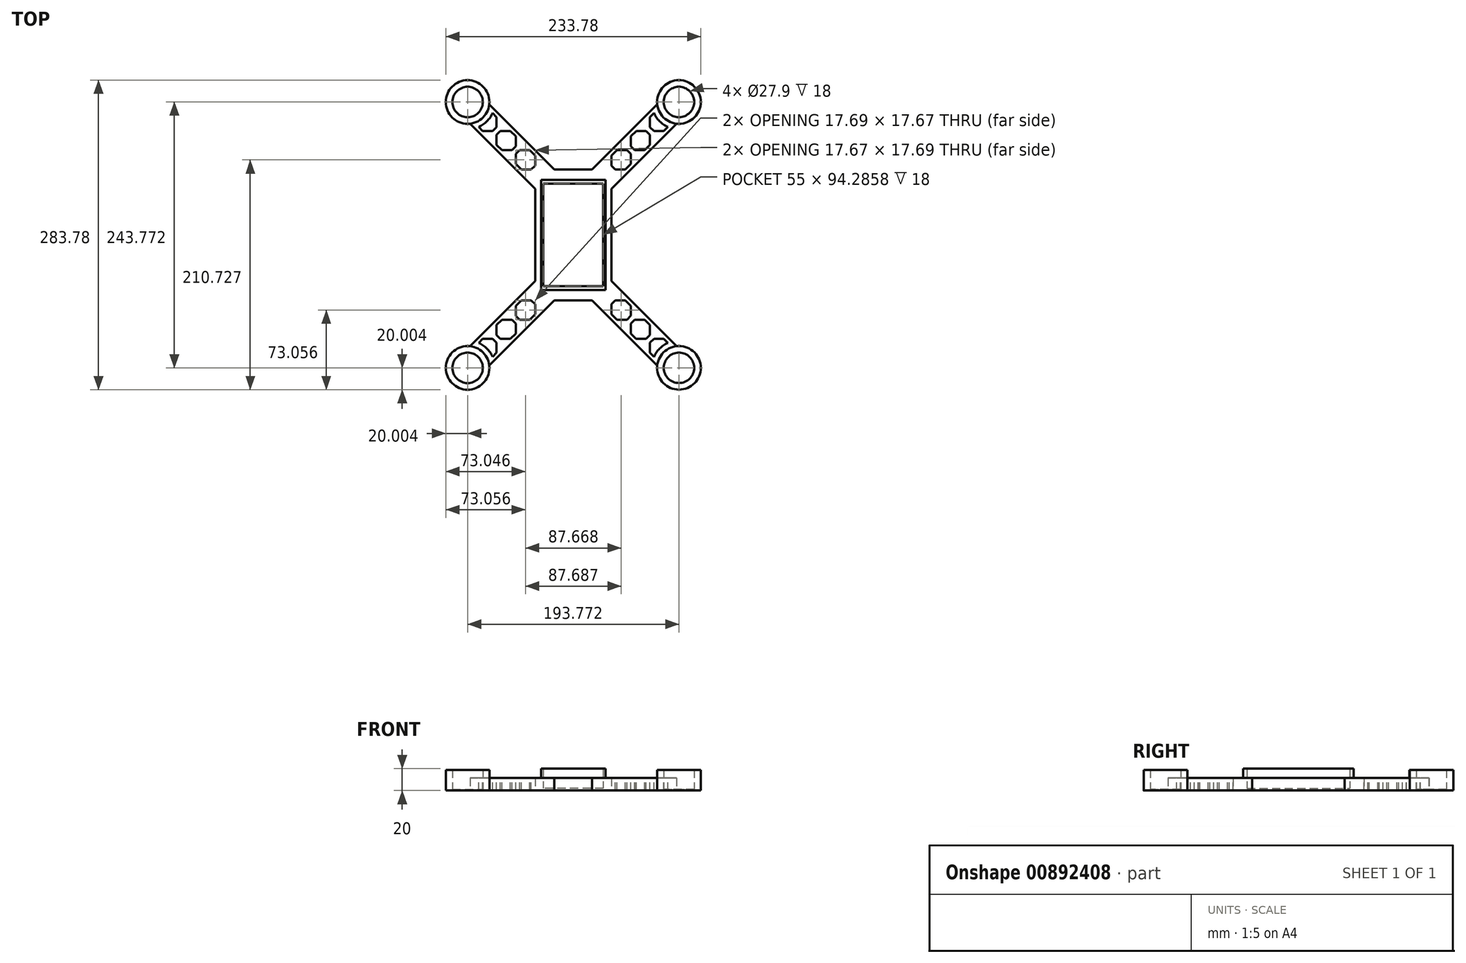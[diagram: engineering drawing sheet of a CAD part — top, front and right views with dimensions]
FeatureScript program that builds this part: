
annotation { "Feature Type Name" : "Feature", "Feature Type Description" : "" }
export const myFeature = defineFeature(function(context is Context, id is Id, definition is map)
    precondition{}
    {
        {
            var Q0;
            Q0=qCreatedBy(makeId("Top.planeOp"),FACE);
            var sketch = newSketch(context, id + "F0", { "sketchPlane" : qUnion([Q0])});
            skLineSegment(sketch, "E0.bottom", {"start": v(-35, 60) * mm, "end": v(35, 60) * mm});
            skLineSegment(sketch, "E0.top", {"start": v(-35, -60) * mm, "end": v(35, -60) * mm});
            skLineSegment(sketch, "E0.left", {"start": v(-35, 60) * mm, "end": v(-35, -60) * mm});
            skLineSegment(sketch, "E0.right", {"start": v(35, 60) * mm, "end": v(35, -60) * mm});
            skPoint(sketch, "E0.middle", {"position": v(0, 0) * mm});
            skPoint(sketch, "E1.middle", {"position": v(-35, 60) * mm});
            skLineSegment(sketch, "E2", {"start": v(-35, 60) * mm, "end": v(35, -60) * mm, "construction": true});
            skLineSegment(sketch, "E3", {"start": v(-35, -60) * mm, "end": v(35, 60) * mm, "construction": true});
            skLineSegment(sketch, "E4", {"start": v(-27.5, 47.14) * mm, "end": v(27.5, 47.14) * mm});
            skLineSegment(sketch, "E5", {"start": v(-27.5, -47.14) * mm, "end": v(27.5, -47.14) * mm});
            skLineSegment(sketch, "E6", {"start": v(27.5, 47.14) * mm, "end": v(27.5, -47.14) * mm});
            skLineSegment(sketch, "E7", {"start": v(-27.5, 47.14) * mm, "end": v(-27.5, -47.14) * mm});
            skPoint(sketch, "E8", {"position": v(-29.52, 50.6) * mm});
            skLineSegment(sketch, "E9", {"start": v(-29.52, 50.6) * mm, "end": v(-29.52, -50.6) * mm});
            skLineSegment(sketch, "E10", {"start": v(-29.52, -50.6) * mm, "end": v(29.52, -50.6) * mm});
            skLineSegment(sketch, "E11", {"start": v(29.52, -50.6) * mm, "end": v(29.52, 50.6) * mm});
            skLineSegment(sketch, "E12", {"start": v(29.52, 50.6) * mm, "end": v(-29.52, 50.6) * mm});
            skLineSegment(sketch, "E13", {"start": v(35, 60) * mm, "end": v(-35, 11.89) * mm, "construction": true});
            skLineSegment(sketch, "E14", {"start": v(35, 11.89) * mm, "end": v(-35, 131.89) * mm, "construction": true});
            skLineSegment(sketch, "E15", {"start": v(-17.33, -60) * mm, "end": v(-35, -42.32) * mm});
            skLineSegment(sketch, "E16", {"start": v(-35, -42.32) * mm, "end": v(-105.72, -113.02) * mm});
            skLineSegment(sketch, "E17", {"start": v(-105.72, -113.02) * mm, "end": v(-88.05, -130.7) * mm});
            skLineSegment(sketch, "E18", {"start": v(-88.05, -130.7) * mm, "end": v(-17.33, -60) * mm});
            skLineSegment(sketch, "E19", {"start": v(105.72, 113.02) * mm, "end": v(88.05, 130.7) * mm});
            skLineSegment(sketch, "E20", {"start": v(88.05, 130.7) * mm, "end": v(17.33, 60) * mm});
            skLineSegment(sketch, "E21", {"start": v(17.33, 60) * mm, "end": v(35, 42.32) * mm});
            skLineSegment(sketch, "E22", {"start": v(35, 42.32) * mm, "end": v(105.72, 113.02) * mm});
            skLineSegment(sketch, "E23", {"start": v(88.05, -130.7) * mm, "end": v(105.72, -113.02) * mm});
            skLineSegment(sketch, "E24", {"start": v(105.72, -113.02) * mm, "end": v(35, -42.32) * mm});
            skLineSegment(sketch, "E25", {"start": v(35, -42.32) * mm, "end": v(17.33, -60) * mm});
            skLineSegment(sketch, "E26", {"start": v(17.33, -60) * mm, "end": v(88.05, -130.7) * mm});
            skLineSegment(sketch, "E27", {"start": v(-35, 42.32) * mm, "end": v(-17.33, 60) * mm});
            skLineSegment(sketch, "E28", {"start": v(-17.33, 60) * mm, "end": v(-88.05, 130.7) * mm});
            skLineSegment(sketch, "E29", {"start": v(-88.05, 130.7) * mm, "end": v(-105.72, 113.02) * mm});
            skLineSegment(sketch, "E30", {"start": v(-105.72, 113.02) * mm, "end": v(-35, 42.32) * mm});
            skLineSegment(sketch, "E31", {"start": v(-35, 42.32) * mm, "end": v(-35, -42.32) * mm});
            skLineSegment(sketch, "E32", {"start": v(-17.33, 60) * mm, "end": v(17.33, 60) * mm});
            skLineSegment(sketch, "E33", {"start": v(35, 42.32) * mm, "end": v(35, -42.32) * mm});
            skSolve(sketch);
        }
        {
            var Q0;
            Q0 = qSketchRegion(id + "F0", true);
            extrude(context, id + "F1", {"entities" : qUnion([Q0]), "depth" : 10 * mm, "offsetDistance" : 25 * mm});
        }
        {
            var Q0;
            Q0=makeQuery(id+"F0.imprint","IMPRINT",FACE,{"disambiguationData":[TD([[makeQuery(id+"F0.imprint","IMPRINT",EDGE,{"derivedFrom":sQuery(id+"F0.wireOp",EDGE,"E4")}),1.0]])]});
            var Q1;
            {var subQ0=sQuery(id+"F0.wireOp",EDGE,"E12");var subQ1=sQuery(id+"F0.wireOp",EDGE,"E9");var subQ2=makeQuery(id+"F0.imprint","INTERSECT",VERTEX,{"derivedFrom":[subQ1,subQ0]});Q1=makeQuery(id+"F0.imprint","IMPRINT",FACE,{"disambiguationData":[TD([[makeQuery(id+"F0.imprint","IMPRINT",EDGE,{"disambiguationData":[TD([[subQ2,-1.0]])],"derivedFrom":subQ1}),1.0]])]});}
            var Q2;
            {var subQ0=sQuery(id+"F0.wireOp",EDGE,"E12");var subQ1=sQuery(id+"F0.wireOp",EDGE,"E11");var subQ2=makeQuery(id+"F0.imprint","INTERSECT",VERTEX,{"derivedFrom":[subQ1,subQ0]});Q2=makeQuery(id+"F0.imprint","IMPRINT",FACE,{"disambiguationData":[TD([[makeQuery(id+"F0.imprint","IMPRINT",EDGE,{"disambiguationData":[TD([[subQ2,1.0]])],"derivedFrom":subQ1}),1.0]])]});}
            var Q3;
            {var subQ0=sQuery(id+"F0.wireOp",EDGE,"E11");var subQ1=sQuery(id+"F0.wireOp",EDGE,"E10");var subQ2=makeQuery(id+"F0.imprint","INTERSECT",VERTEX,{"derivedFrom":[subQ1,subQ0]});Q3=makeQuery(id+"F0.imprint","IMPRINT",FACE,{"disambiguationData":[TD([[makeQuery(id+"F0.imprint","IMPRINT",EDGE,{"disambiguationData":[TD([[subQ2,1.0]])],"derivedFrom":subQ1}),1.0]])]});}
            var Q4;
            {var subQ0=sQuery(id+"F0.wireOp",EDGE,"E10");var subQ1=sQuery(id+"F0.wireOp",EDGE,"E9");var subQ2=makeQuery(id+"F0.imprint","INTERSECT",VERTEX,{"derivedFrom":[subQ1,subQ0]});Q4=makeQuery(id+"F0.imprint","IMPRINT",FACE,{"disambiguationData":[TD([[makeQuery(id+"F0.imprint","IMPRINT",EDGE,{"disambiguationData":[TD([[subQ2,1.0]])],"derivedFrom":subQ1}),1.0]])]});}
            extrude(context, id + "F2", {"entities" : qUnion([Q0, Q1, Q2, Q3, Q4]), "operationType" : NewBodyOperationType.ADD, "depth" : 20 * mm, "offsetDistance" : 25 * mm});
        }
        {
            var Q0;
            Q0=makeQuery(id+"F0.imprint","IMPRINT",FACE,{"disambiguationData":[TD([[makeQuery(id+"F0.imprint","IMPRINT",EDGE,{"derivedFrom":sQuery(id+"F0.wireOp",EDGE,"E4")}),-1.0]])]});
            extrude(context, id + "F3", {"entities" : qUnion([Q0]), "operationType" : NewBodyOperationType.ADD, "depth" : 3 * mm, "offsetDistance" : 25 * mm});
        }
        {
            var Q0;
            {var subQ0=sQuery(id+"F0.wireOp",EDGE,"E7");var subQ1=sQuery(id+"F0.wireOp",EDGE,"E6");var subQ2=sQuery(id+"F0.wireOp",EDGE,"E5");var subQ3=sQuery(id+"F0.wireOp",EDGE,"E4");var subQ4=sQuery(id+"F0.wireOp",EDGE,"E12");var subQ5=sQuery(id+"F0.wireOp",EDGE,"E11");var subQ6=sQuery(id+"F0.wireOp",EDGE,"E10");var subQ7=sQuery(id+"F0.wireOp",EDGE,"E9");Q0=makeQuery(id+"F3.boolean.opBoolean","MERGE",FACE,{"derivedFrom":[makeQuery(id+"F2.boolean.opBoolean","MERGE",FACE,{"derivedFrom":[makeQuery(id+"F1.opExtrude","CAP_FACE",FACE,{"disambiguationData":[OSD([sQuery(id+"F0.wireOp",EDGE,"E0.top"),subQ7,subQ6,subQ5,subQ4,sQuery(id+"F0.wireOp",EDGE,"E16"),sQuery(id+"F0.wireOp",EDGE,"E17"),sQuery(id+"F0.wireOp",EDGE,"E18"),sQuery(id+"F0.wireOp",EDGE,"E19"),sQuery(id+"F0.wireOp",EDGE,"E20"),sQuery(id+"F0.wireOp",EDGE,"E22"),sQuery(id+"F0.wireOp",EDGE,"E23"),sQuery(id+"F0.wireOp",EDGE,"E24"),sQuery(id+"F0.wireOp",EDGE,"E26"),sQuery(id+"F0.wireOp",EDGE,"E28"),sQuery(id+"F0.wireOp",EDGE,"E29"),sQuery(id+"F0.wireOp",EDGE,"E30"),sQuery(id+"F0.wireOp",EDGE,"E31"),sQuery(id+"F0.wireOp",EDGE,"E32"),sQuery(id+"F0.wireOp",EDGE,"E33")])],"isStart":true}),makeQuery(id+"F2.opExtrude","CAP_FACE",FACE,{"disambiguationData":[OSD([subQ3,subQ2,subQ1,subQ0,subQ7,subQ6,subQ5,subQ4])],"isStart":true})]}),makeQuery(id+"F3.opExtrude","CAP_FACE",FACE,{"disambiguationData":[OSD([subQ3,subQ2,subQ1,subQ0])],"isStart":true})]});}
            var sketch = newSketch(context, id + "F4", { "sketchPlane" : qUnion([Q0])});
            skLineSegment(sketch, "E34", {"start": v(-35, 42.32) * mm, "end": v(35, 42.32) * mm, "construction": true});
            skLineSegment(sketch, "E35", {"start": v(35, -42.32) * mm, "end": v(-35, -42.32) * mm, "construction": true});
            skLineSegment(sketch, "E36", {"start": v(0, 42.32) * mm, "end": v(0, -42.32) * mm, "construction": true});
            skLineSegment(sketch, "E37", {"start": v(-30, 42.32) * mm, "end": v(-30, -42.32) * mm});
            skLineSegment(sketch, "E38", {"start": v(-30, -42.32) * mm, "end": v(-27, -42.32) * mm, "construction": true});
            skLineSegment(sketch, "E39", {"start": v(-27, -42.32) * mm, "end": v(-27, 42.32) * mm});
            skLineSegment(sketch, "E40", {"start": v(-27, 42.32) * mm, "end": v(-30, 42.32) * mm});
            skLineSegment(sketch, "E41", {"start": v(-30, -42.32) * mm, "end": v(-27, -42.32) * mm});
            skLineSegment(sketch, "E42.MirrorCS", {"start": v(30, 42.32) * mm, "end": v(30, -42.32) * mm});
            skLineSegment(sketch, "E43.MirrorCS", {"start": v(27, -42.32) * mm, "end": v(27, 42.32) * mm});
            skLineSegment(sketch, "E44", {"start": v(30, 42.32) * mm, "end": v(27, 42.32) * mm});
            skLineSegment(sketch, "E45", {"start": v(27, -42.32) * mm, "end": v(30, -42.32) * mm});
            skSolve(sketch);
        }
        {
            var Q0;
            {var subQ0=sQuery(id+"F0.wireOp",EDGE,"E7");var subQ1=sQuery(id+"F0.wireOp",EDGE,"E6");var subQ2=sQuery(id+"F0.wireOp",EDGE,"E5");var subQ3=sQuery(id+"F0.wireOp",EDGE,"E4");var subQ4=sQuery(id+"F0.wireOp",EDGE,"E12");var subQ5=sQuery(id+"F0.wireOp",EDGE,"E11");var subQ6=sQuery(id+"F0.wireOp",EDGE,"E10");var subQ7=sQuery(id+"F0.wireOp",EDGE,"E9");Q0=makeQuery(id+"F3.boolean.opBoolean","MERGE",FACE,{"derivedFrom":[makeQuery(id+"F2.boolean.opBoolean","MERGE",FACE,{"derivedFrom":[makeQuery(id+"F1.opExtrude","CAP_FACE",FACE,{"disambiguationData":[OSD([sQuery(id+"F0.wireOp",EDGE,"E0.top"),subQ7,subQ6,subQ5,subQ4,sQuery(id+"F0.wireOp",EDGE,"E16"),sQuery(id+"F0.wireOp",EDGE,"E17"),sQuery(id+"F0.wireOp",EDGE,"E18"),sQuery(id+"F0.wireOp",EDGE,"E19"),sQuery(id+"F0.wireOp",EDGE,"E20"),sQuery(id+"F0.wireOp",EDGE,"E22"),sQuery(id+"F0.wireOp",EDGE,"E23"),sQuery(id+"F0.wireOp",EDGE,"E24"),sQuery(id+"F0.wireOp",EDGE,"E26"),sQuery(id+"F0.wireOp",EDGE,"E28"),sQuery(id+"F0.wireOp",EDGE,"E29"),sQuery(id+"F0.wireOp",EDGE,"E30"),sQuery(id+"F0.wireOp",EDGE,"E31"),sQuery(id+"F0.wireOp",EDGE,"E32"),sQuery(id+"F0.wireOp",EDGE,"E33")])],"isStart":true}),makeQuery(id+"F2.opExtrude","CAP_FACE",FACE,{"disambiguationData":[OSD([subQ3,subQ2,subQ1,subQ0,subQ7,subQ6,subQ5,subQ4])],"isStart":true})]}),makeQuery(id+"F3.opExtrude","CAP_FACE",FACE,{"disambiguationData":[OSD([subQ3,subQ2,subQ1,subQ0])],"isStart":true})]});}
            var sketch = newSketch(context, id + "F5", { "sketchPlane" : qUnion([Q0])});
            skCircle(sketch, "E46", {"center": v(96.89, 121.86) * mm, "radius": 13.95 * mm});
            skCircle(sketch, "E47", {"center": v(96.89, 121.86) * mm, "radius": 20 * mm});
            skLineSegment(sketch, "E48", {"start": v(88.05, 130.7) * mm, "end": v(111.03, 107.71) * mm, "construction": true});
            skCircle(sketch, "E49", {"center": v(-96.86, 121.89) * mm, "radius": 13.95 * mm});
            skCircle(sketch, "E50", {"center": v(-96.86, 121.89) * mm, "radius": 20 * mm});
            skCircle(sketch, "E51", {"center": v(96.86, -121.89) * mm, "radius": 13.95 * mm});
            skCircle(sketch, "E52", {"center": v(96.86, -121.89) * mm, "radius": 20 * mm});
            skCircle(sketch, "E53", {"center": v(-96.89, -121.86) * mm, "radius": 13.95 * mm});
            skCircle(sketch, "E54", {"center": v(-96.89, -121.86) * mm, "radius": 20 * mm});
            skSolve(sketch);
        }
        {
            var Q0;
            {var subQ0=sQuery(id+"F5.wireOp",EDGE,"47fc8cb0-7b7c-463f-8738-2b292fe60b7a0.MirrorCS");var subQ1=sQuery(id+"F5.wireOp",EDGE,"E47");var subQ2=makeQuery(id+"F5.imprint","INTERSECT",VERTEX,{"disambiguationData":[OD(1.0)],"derivedFrom":[subQ1,subQ0]});Q0=makeQuery(id+"F5.imprint","IMPRINT",FACE,{"disambiguationData":[TD([[makeQuery(id+"F5.imprint","IMPRINT",EDGE,{"disambiguationData":[TD([[subQ2,-1.0]])],"derivedFrom":subQ1}),-1.0]])]});}
            var Q1;
            {var subQ0=sQuery(id+"F5.wireOp",EDGE,"VyiwcckC-eZpB-Ns7w-MLVF-TjthNmdLp171");var subQ1=sQuery(id+"F5.wireOp",EDGE,"E47");var subQ2=makeQuery(id+"F5.imprint","INTERSECT",VERTEX,{"disambiguationData":[OD(1.0)],"derivedFrom":[subQ1,subQ0]});Q1=makeQuery(id+"F5.imprint","IMPRINT",FACE,{"disambiguationData":[TD([[makeQuery(id+"F5.imprint","IMPRINT",EDGE,{"disambiguationData":[TD([[subQ2,1.0]])],"derivedFrom":subQ1}),-1.0]])]});}
            var Q2;
            {var subQ6=makeQuery(id+"F1.opExtrude","CAP_EDGE",EDGE,{"disambiguationData":[OSD([sQuery(id+"F0.wireOp",EDGE,"E24")])],"isStart":true});var subQ11=sQuery(id+"F5.wireOp",EDGE,"E46");var subQ12=makeQuery(id+"F5.imprint","INTERSECT",VERTEX,{"derivedFrom":[subQ6,subQ11]});Q2=makeQuery(id+"F5.imprint","IMPRINT",FACE,{"disambiguationData":[TD([[makeQuery(id+"F5.imprint","IMPRINT",EDGE,{"disambiguationData":[TD([[subQ12,-1.0]])],"derivedFrom":subQ11}),-1.0]])]});}
            var Q3;
            {var subQ0=sQuery(id+"F5.wireOp",EDGE,"E46");var subQ1=makeQuery(id+"F1.opExtrude","CAP_EDGE",EDGE,{"disambiguationData":[OSD([sQuery(id+"F0.wireOp",EDGE,"E24")])],"isStart":true});var subQ2=makeQuery(id+"F5.imprint","INTERSECT",VERTEX,{"derivedFrom":[subQ1,subQ0]});Q3=makeQuery(id+"F5.imprint","IMPRINT",FACE,{"disambiguationData":[TD([[makeQuery(id+"F5.imprint","IMPRINT",EDGE,{"disambiguationData":[TD([[subQ2,1.0]])],"derivedFrom":subQ0}),-1.0]])]});}
            extrude(context, id + "F6", {"entities" : qUnion([Q0, Q1, Q2, Q3]), "operationType" : NewBodyOperationType.ADD, "depth" : -18 * mm, "offsetDistance" : 25 * mm});
        }
        {
            var Q0;
            {var subQ8=sQuery(id+"F5.wireOp",EDGE,"E49");var subQ11=makeQuery(id+"F1.opExtrude","CAP_EDGE",EDGE,{"disambiguationData":[OSD([sQuery(id+"F0.wireOp",EDGE,"E16")])],"isStart":true});var subQ13=makeQuery(id+"F5.imprint","INTERSECT",VERTEX,{"derivedFrom":[subQ11,subQ8]});Q0=makeQuery(id+"F5.imprint","IMPRINT",FACE,{"disambiguationData":[TD([[makeQuery(id+"F5.imprint","IMPRINT",EDGE,{"disambiguationData":[TD([[subQ13,1.0]])],"derivedFrom":subQ8}),-1.0]])]});}
            var Q1;
            {var subQ0=sQuery(id+"F5.wireOp",EDGE,"3d39e784-e424-4d79-a023-b1c7c5447e9a.MirrorCS");var subQ1=sQuery(id+"F5.wireOp",EDGE,"E50");var subQ2=makeQuery(id+"F5.imprint","INTERSECT",VERTEX,{"disambiguationData":[OD(1.0)],"derivedFrom":[subQ1,subQ0]});Q1=makeQuery(id+"F5.imprint","IMPRINT",FACE,{"disambiguationData":[TD([[makeQuery(id+"F5.imprint","IMPRINT",EDGE,{"disambiguationData":[TD([[subQ2,-1.0]])],"derivedFrom":subQ1}),-1.0]])]});}
            var Q2;
            {var subQ0=sQuery(id+"F5.wireOp",EDGE,"9ff1a962-2a44-446a-a701-eef2fafc3d29");var subQ1=sQuery(id+"F5.wireOp",EDGE,"E50");var subQ2=makeQuery(id+"F5.imprint","INTERSECT",VERTEX,{"disambiguationData":[OD(1.0)],"derivedFrom":[subQ1,subQ0]});Q2=makeQuery(id+"F5.imprint","IMPRINT",FACE,{"disambiguationData":[TD([[makeQuery(id+"F5.imprint","IMPRINT",EDGE,{"disambiguationData":[TD([[subQ2,1.0]])],"derivedFrom":subQ1}),-1.0]])]});}
            var Q3;
            {var subQ0=sQuery(id+"F5.wireOp",EDGE,"E49");var subQ1=makeQuery(id+"F1.opExtrude","CAP_EDGE",EDGE,{"disambiguationData":[OSD([sQuery(id+"F0.wireOp",EDGE,"E16")])],"isStart":true});var subQ2=makeQuery(id+"F5.imprint","INTERSECT",VERTEX,{"derivedFrom":[subQ1,subQ0]});Q3=makeQuery(id+"F5.imprint","IMPRINT",FACE,{"disambiguationData":[TD([[makeQuery(id+"F5.imprint","IMPRINT",EDGE,{"disambiguationData":[TD([[subQ2,-1.0]])],"derivedFrom":subQ0}),-1.0]])]});}
            var Q4;
            {var subQ0=sQuery(id+"F5.wireOp",EDGE,"47fc8cb0-7b7c-463f-8738-2b292fe60b7a0.MirrorCS");var subQ1=sQuery(id+"F5.wireOp",EDGE,"E47");var subQ2=makeQuery(id+"F5.imprint","INTERSECT",VERTEX,{"disambiguationData":[OD(1.0)],"derivedFrom":[subQ1,subQ0]});Q4=makeQuery(id+"F5.imprint","IMPRINT",FACE,{"disambiguationData":[TD([[makeQuery(id+"F5.imprint","IMPRINT",EDGE,{"disambiguationData":[TD([[subQ2,-1.0]])],"derivedFrom":subQ1}),-1.0]])]});}
            var Q5;
            {var subQ0=sQuery(id+"F5.wireOp",EDGE,"E46");var subQ1=makeQuery(id+"F1.opExtrude","CAP_EDGE",EDGE,{"disambiguationData":[OSD([sQuery(id+"F0.wireOp",EDGE,"E24")])],"isStart":true});var subQ2=makeQuery(id+"F5.imprint","INTERSECT",VERTEX,{"derivedFrom":[subQ1,subQ0]});Q5=makeQuery(id+"F5.imprint","IMPRINT",FACE,{"disambiguationData":[TD([[makeQuery(id+"F5.imprint","IMPRINT",EDGE,{"disambiguationData":[TD([[subQ2,1.0]])],"derivedFrom":subQ0}),-1.0]])]});}
            var Q6;
            {var subQ0=sQuery(id+"F5.wireOp",EDGE,"VyiwcckC-eZpB-Ns7w-MLVF-TjthNmdLp171");var subQ1=sQuery(id+"F5.wireOp",EDGE,"E47");var subQ2=makeQuery(id+"F5.imprint","INTERSECT",VERTEX,{"disambiguationData":[OD(1.0)],"derivedFrom":[subQ1,subQ0]});Q6=makeQuery(id+"F5.imprint","IMPRINT",FACE,{"disambiguationData":[TD([[makeQuery(id+"F5.imprint","IMPRINT",EDGE,{"disambiguationData":[TD([[subQ2,1.0]])],"derivedFrom":subQ1}),-1.0]])]});}
            var Q7;
            {var subQ7=sQuery(id+"F5.wireOp",EDGE,"E46");var subQ10=makeQuery(id+"F1.opExtrude","CAP_EDGE",EDGE,{"disambiguationData":[OSD([sQuery(id+"F0.wireOp",EDGE,"E24")])],"isStart":true});var subQ13=makeQuery(id+"F5.imprint","INTERSECT",VERTEX,{"derivedFrom":[subQ10,subQ7]});Q7=makeQuery(id+"F5.imprint","IMPRINT",FACE,{"disambiguationData":[TD([[makeQuery(id+"F5.imprint","IMPRINT",EDGE,{"disambiguationData":[TD([[subQ13,-1.0]])],"derivedFrom":subQ7}),-1.0]])]});}
            var Q8;
            {var subQ6=makeQuery(id+"F1.opExtrude","CAP_EDGE",EDGE,{"disambiguationData":[OSD([sQuery(id+"F0.wireOp",EDGE,"E20")])],"isStart":true});var subQ11=sQuery(id+"F5.wireOp",EDGE,"E51");var subQ12=makeQuery(id+"F5.imprint","INTERSECT",VERTEX,{"derivedFrom":[subQ6,subQ11]});Q8=makeQuery(id+"F5.imprint","IMPRINT",FACE,{"disambiguationData":[TD([[makeQuery(id+"F5.imprint","IMPRINT",EDGE,{"disambiguationData":[TD([[subQ12,-1.0]])],"derivedFrom":subQ11}),-1.0]])]});}
            var Q9;
            {var subQ0=sQuery(id+"F5.wireOp",EDGE,"E51");var subQ1=makeQuery(id+"F1.opExtrude","CAP_EDGE",EDGE,{"disambiguationData":[OSD([sQuery(id+"F0.wireOp",EDGE,"E20")])],"isStart":true});var subQ2=makeQuery(id+"F5.imprint","INTERSECT",VERTEX,{"derivedFrom":[subQ1,subQ0]});Q9=makeQuery(id+"F5.imprint","IMPRINT",FACE,{"disambiguationData":[TD([[makeQuery(id+"F5.imprint","IMPRINT",EDGE,{"disambiguationData":[TD([[subQ2,1.0]])],"derivedFrom":subQ0}),-1.0]])]});}
            var Q10;
            {var subQ0=sQuery(id+"F5.wireOp",EDGE,"61715c0d-76a2-4f19-8c7d-4868fa988be3");var subQ1=sQuery(id+"F5.wireOp",EDGE,"E52");var subQ2=makeQuery(id+"F5.imprint","INTERSECT",VERTEX,{"disambiguationData":[OD(1.0)],"derivedFrom":[subQ1,subQ0]});Q10=makeQuery(id+"F5.imprint","IMPRINT",FACE,{"disambiguationData":[TD([[makeQuery(id+"F5.imprint","IMPRINT",EDGE,{"disambiguationData":[TD([[subQ2,1.0]])],"derivedFrom":subQ1}),-1.0]])]});}
            var Q11;
            {var subQ0=sQuery(id+"F5.wireOp",EDGE,"6347a85b-d320-4235-87b3-466630833275.MirrorCS");var subQ1=sQuery(id+"F5.wireOp",EDGE,"E52");var subQ2=makeQuery(id+"F5.imprint","INTERSECT",VERTEX,{"disambiguationData":[OD(1.0)],"derivedFrom":[subQ1,subQ0]});Q11=makeQuery(id+"F5.imprint","IMPRINT",FACE,{"disambiguationData":[TD([[makeQuery(id+"F5.imprint","IMPRINT",EDGE,{"disambiguationData":[TD([[subQ2,-1.0]])],"derivedFrom":subQ1}),-1.0]])]});}
            var Q12;
            {var subQ0=sQuery(id+"F5.wireOp",EDGE,"E53");var subQ1=makeQuery(id+"F1.opExtrude","CAP_EDGE",EDGE,{"disambiguationData":[OSD([sQuery(id+"F0.wireOp",EDGE,"E28")])],"isStart":true});var subQ2=makeQuery(id+"F5.imprint","INTERSECT",VERTEX,{"derivedFrom":[subQ1,subQ0]});Q12=makeQuery(id+"F5.imprint","IMPRINT",FACE,{"disambiguationData":[TD([[makeQuery(id+"F5.imprint","IMPRINT",EDGE,{"disambiguationData":[TD([[subQ2,-1.0]])],"derivedFrom":subQ0}),-1.0]])]});}
            var Q13;
            {var subQ0=sQuery(id+"F5.wireOp",EDGE,"2b9b2cda-c36c-46c9-b2f3-9b1550c60cb7.MirrorCS");var subQ1=sQuery(id+"F5.wireOp",EDGE,"E54");var subQ2=makeQuery(id+"F5.imprint","INTERSECT",VERTEX,{"disambiguationData":[OD(1.0)],"derivedFrom":[subQ1,subQ0]});Q13=makeQuery(id+"F5.imprint","IMPRINT",FACE,{"disambiguationData":[TD([[makeQuery(id+"F5.imprint","IMPRINT",EDGE,{"disambiguationData":[TD([[subQ2,-1.0]])],"derivedFrom":subQ1}),-1.0]])]});}
            var Q14;
            {var subQ8=makeQuery(id+"F1.opExtrude","CAP_EDGE",EDGE,{"disambiguationData":[OSD([sQuery(id+"F0.wireOp",EDGE,"E28")])],"isStart":true});var subQ10=sQuery(id+"F5.wireOp",EDGE,"E53");var subQ11=makeQuery(id+"F5.imprint","INTERSECT",VERTEX,{"derivedFrom":[subQ8,subQ10]});Q14=makeQuery(id+"F5.imprint","IMPRINT",FACE,{"disambiguationData":[TD([[makeQuery(id+"F5.imprint","IMPRINT",EDGE,{"disambiguationData":[TD([[subQ11,1.0]])],"derivedFrom":subQ10}),-1.0]])]});}
            var Q15;
            {var subQ0=sQuery(id+"F5.wireOp",EDGE,"51958e25-218a-4250-a5e8-a469592214fb");var subQ1=sQuery(id+"F5.wireOp",EDGE,"E54");var subQ2=makeQuery(id+"F5.imprint","INTERSECT",VERTEX,{"disambiguationData":[OD(1.0)],"derivedFrom":[subQ1,subQ0]});Q15=makeQuery(id+"F5.imprint","IMPRINT",FACE,{"disambiguationData":[TD([[makeQuery(id+"F5.imprint","IMPRINT",EDGE,{"disambiguationData":[TD([[subQ2,1.0]])],"derivedFrom":subQ1}),-1.0]])]});}
            extrude(context, id + "F7", {"entities" : qUnion([Q0, Q1, Q2, Q3, Q4, Q5, Q6, Q7, Q8, Q9, Q10, Q11, Q12, Q13, Q14, Q15]), "operationType" : NewBodyOperationType.ADD, "depth" : -19 * mm, "offsetDistance" : 25 * mm});
        }
        {
            var Q0;
            {var subQ0=sQuery(id+"F0.wireOp",EDGE,"E28");var subQ1=makeQuery(id+"F1.opExtrude","SWEPT_FACE",FACE,{"disambiguationData":[OSD([subQ0])]});var subQ2=sQuery(id+"F0.wireOp",EDGE,"E29");var subQ4=sQuery(id+"F0.wireOp",EDGE,"E30");var subQ6=sQuery(id+"F0.wireOp",EDGE,"E11");var subQ7=sQuery(id+"F0.wireOp",EDGE,"E10");var subQ8=sQuery(id+"F0.wireOp",EDGE,"E22");var subQ9=sQuery(id+"F0.wireOp",EDGE,"E19");var subQ10=sQuery(id+"F0.wireOp",EDGE,"E26");var subQ11=sQuery(id+"F0.wireOp",EDGE,"E20");var subQ12=sQuery(id+"F0.wireOp",EDGE,"E0.top");var subQ13=sQuery(id+"F0.wireOp",EDGE,"E12");var subQ14=sQuery(id+"F0.wireOp",EDGE,"E16");var subQ15=sQuery(id+"F0.wireOp",EDGE,"E17");var subQ16=sQuery(id+"F0.wireOp",EDGE,"E18");var subQ17=sQuery(id+"F0.wireOp",EDGE,"E24");var subQ18=sQuery(id+"F0.wireOp",EDGE,"E31");var subQ19=sQuery(id+"F0.wireOp",EDGE,"E32");var subQ20=sQuery(id+"F0.wireOp",EDGE,"E33");var subQ21=sQuery(id+"F0.wireOp",EDGE,"E9");Q0=makeQuery(id+"F7.boolean.opBoolean","SPLIT",FACE,{"disambiguationData":[TD([subQ1])],"derivedFrom":makeQuery(id+"F6.boolean.opBoolean","SPLIT",FACE,{"disambiguationData":[TD([makeQuery(id+"F1.opExtrude","SWEPT_FACE",FACE,{"disambiguationData":[OSD([subQ12])]})])],"derivedFrom":makeQuery(id+"F1.opExtrude","CAP_FACE",FACE,{"disambiguationData":[OSD([subQ12,subQ21,subQ7,subQ6,subQ13,subQ14,subQ15,subQ16,subQ9,subQ11,subQ8,sQuery(id+"F0.wireOp",EDGE,"E23"),subQ17,subQ10,subQ0,subQ2,subQ4,subQ18,subQ19,subQ20])],"isStart":false})})});}
            var Q1;
            {var subQ0=sQuery(id+"F0.wireOp",EDGE,"E16");var subQ2=sQuery(id+"F0.wireOp",EDGE,"E17");var subQ3=makeQuery(id+"F1.opExtrude","SWEPT_FACE",FACE,{"disambiguationData":[OSD([subQ2])]});var subQ4=sQuery(id+"F0.wireOp",EDGE,"E18");var subQ6=sQuery(id+"F0.wireOp",EDGE,"E29");var subQ7=sQuery(id+"F0.wireOp",EDGE,"E11");var subQ8=sQuery(id+"F0.wireOp",EDGE,"E28");var subQ9=sQuery(id+"F0.wireOp",EDGE,"E10");var subQ10=sQuery(id+"F0.wireOp",EDGE,"E22");var subQ11=sQuery(id+"F0.wireOp",EDGE,"E19");var subQ12=sQuery(id+"F0.wireOp",EDGE,"E26");var subQ13=sQuery(id+"F0.wireOp",EDGE,"E20");var subQ14=sQuery(id+"F0.wireOp",EDGE,"E0.top");var subQ15=sQuery(id+"F0.wireOp",EDGE,"E30");var subQ16=sQuery(id+"F0.wireOp",EDGE,"E12");var subQ17=sQuery(id+"F0.wireOp",EDGE,"E24");var subQ18=sQuery(id+"F0.wireOp",EDGE,"E31");var subQ19=sQuery(id+"F0.wireOp",EDGE,"E32");var subQ20=sQuery(id+"F0.wireOp",EDGE,"E33");var subQ21=sQuery(id+"F0.wireOp",EDGE,"E9");Q1=makeQuery(id+"F7.boolean.opBoolean","SPLIT",FACE,{"disambiguationData":[TD([subQ3])],"derivedFrom":makeQuery(id+"F6.boolean.opBoolean","SPLIT",FACE,{"disambiguationData":[TD([makeQuery(id+"F1.opExtrude","SWEPT_FACE",FACE,{"disambiguationData":[OSD([subQ14])]})])],"derivedFrom":makeQuery(id+"F1.opExtrude","CAP_FACE",FACE,{"disambiguationData":[OSD([subQ14,subQ21,subQ9,subQ7,subQ16,subQ0,subQ2,subQ4,subQ11,subQ13,subQ10,sQuery(id+"F0.wireOp",EDGE,"E23"),subQ17,subQ12,subQ8,subQ6,subQ15,subQ18,subQ19,subQ20])],"isStart":false})})});}
            var Q2;
            {var subQ0=sQuery(id+"F0.wireOp",EDGE,"E23");var subQ1=sQuery(id+"F0.wireOp",EDGE,"E24");var subQ2=sQuery(id+"F0.wireOp",EDGE,"E26");Q2=makeQuery(id+"F6.boolean.opBoolean","SPLIT",FACE,{"disambiguationData":[TD([makeQuery(id+"F1.opExtrude","SWEPT_FACE",FACE,{"disambiguationData":[OSD([subQ0])]})])],"derivedFrom":makeQuery(id+"F1.opExtrude","CAP_FACE",FACE,{"disambiguationData":[OSD([sQuery(id+"F0.wireOp",EDGE,"E0.top"),sQuery(id+"F0.wireOp",EDGE,"E9"),sQuery(id+"F0.wireOp",EDGE,"E10"),sQuery(id+"F0.wireOp",EDGE,"E11"),sQuery(id+"F0.wireOp",EDGE,"E12"),sQuery(id+"F0.wireOp",EDGE,"E16"),sQuery(id+"F0.wireOp",EDGE,"E17"),sQuery(id+"F0.wireOp",EDGE,"E18"),sQuery(id+"F0.wireOp",EDGE,"E19"),sQuery(id+"F0.wireOp",EDGE,"E20"),sQuery(id+"F0.wireOp",EDGE,"E22"),subQ0,subQ1,subQ2,sQuery(id+"F0.wireOp",EDGE,"E28"),sQuery(id+"F0.wireOp",EDGE,"E29"),sQuery(id+"F0.wireOp",EDGE,"E30"),sQuery(id+"F0.wireOp",EDGE,"E31"),sQuery(id+"F0.wireOp",EDGE,"E32"),sQuery(id+"F0.wireOp",EDGE,"E33")])],"isStart":false})});}
            var Q3;
            {var subQ0=sQuery(id+"F0.wireOp",EDGE,"E19");var subQ1=makeQuery(id+"F1.opExtrude","SWEPT_FACE",FACE,{"disambiguationData":[OSD([subQ0])]});var subQ2=sQuery(id+"F0.wireOp",EDGE,"E20");var subQ4=sQuery(id+"F0.wireOp",EDGE,"E22");var subQ6=sQuery(id+"F0.wireOp",EDGE,"E29");var subQ7=sQuery(id+"F0.wireOp",EDGE,"E11");var subQ8=sQuery(id+"F0.wireOp",EDGE,"E28");var subQ9=sQuery(id+"F0.wireOp",EDGE,"E10");var subQ10=sQuery(id+"F0.wireOp",EDGE,"E26");var subQ11=sQuery(id+"F0.wireOp",EDGE,"E0.top");var subQ12=sQuery(id+"F0.wireOp",EDGE,"E30");var subQ13=sQuery(id+"F0.wireOp",EDGE,"E12");var subQ14=sQuery(id+"F0.wireOp",EDGE,"E16");var subQ15=sQuery(id+"F0.wireOp",EDGE,"E17");var subQ16=sQuery(id+"F0.wireOp",EDGE,"E18");var subQ17=sQuery(id+"F0.wireOp",EDGE,"E24");var subQ18=sQuery(id+"F0.wireOp",EDGE,"E31");var subQ19=sQuery(id+"F0.wireOp",EDGE,"E32");var subQ20=sQuery(id+"F0.wireOp",EDGE,"E33");var subQ21=sQuery(id+"F0.wireOp",EDGE,"E9");Q3=makeQuery(id+"F7.boolean.opBoolean","SPLIT",FACE,{"disambiguationData":[TD([subQ1])],"derivedFrom":makeQuery(id+"F6.boolean.opBoolean","SPLIT",FACE,{"disambiguationData":[TD([makeQuery(id+"F1.opExtrude","SWEPT_FACE",FACE,{"disambiguationData":[OSD([subQ11])]})])],"derivedFrom":makeQuery(id+"F1.opExtrude","CAP_FACE",FACE,{"disambiguationData":[OSD([subQ11,subQ21,subQ9,subQ7,subQ13,subQ14,subQ15,subQ16,subQ0,subQ2,subQ4,sQuery(id+"F0.wireOp",EDGE,"E23"),subQ17,subQ10,subQ8,subQ6,subQ12,subQ18,subQ19,subQ20])],"isStart":false})})});}
            extrude(context, id + "F8", {"entities" : qUnion([Q0, Q1, Q2, Q3]), "operationType" : NewBodyOperationType.REMOVE, "oppositeDirection" : true, "depth" : 25 * mm, "offsetDistance" : 25 * mm});
        }
        {
            var Q0;
            {var subQ0=sQuery(id+"F0.wireOp",EDGE,"E30");var subQ1=sQuery(id+"F0.wireOp",EDGE,"E28");var subQ2=sQuery(id+"F0.wireOp",EDGE,"E22");var subQ3=sQuery(id+"F0.wireOp",EDGE,"E20");var subQ4=sQuery(id+"F0.wireOp",EDGE,"E18");var subQ5=sQuery(id+"F0.wireOp",EDGE,"E16");var subQ6=sQuery(id+"F0.wireOp",EDGE,"E26");var subQ7=sQuery(id+"F0.wireOp",EDGE,"E24");var subQ8=sQuery(id+"F0.wireOp",EDGE,"E7");var subQ9=sQuery(id+"F0.wireOp",EDGE,"E6");var subQ10=sQuery(id+"F0.wireOp",EDGE,"E5");var subQ11=sQuery(id+"F0.wireOp",EDGE,"E4");var subQ12=sQuery(id+"F0.wireOp",EDGE,"E12");var subQ13=sQuery(id+"F0.wireOp",EDGE,"E11");var subQ14=sQuery(id+"F0.wireOp",EDGE,"E10");var subQ15=sQuery(id+"F0.wireOp",EDGE,"E9");Q0=makeQuery(id+"F7.boolean.opBoolean","MERGE",FACE,{"derivedFrom":[makeQuery(id+"F6.boolean.opBoolean","MERGE",FACE,{"derivedFrom":[makeQuery(id+"F3.boolean.opBoolean","MERGE",FACE,{"derivedFrom":[makeQuery(id+"F2.boolean.opBoolean","MERGE",FACE,{"derivedFrom":[makeQuery(id+"F1.opExtrude","CAP_FACE",FACE,{"disambiguationData":[OSD([sQuery(id+"F0.wireOp",EDGE,"E0.top"),subQ15,subQ14,subQ13,subQ12,subQ5,sQuery(id+"F0.wireOp",EDGE,"E17"),subQ4,sQuery(id+"F0.wireOp",EDGE,"E19"),subQ3,subQ2,sQuery(id+"F0.wireOp",EDGE,"E23"),subQ7,subQ6,subQ1,sQuery(id+"F0.wireOp",EDGE,"E29"),subQ0,sQuery(id+"F0.wireOp",EDGE,"E31"),sQuery(id+"F0.wireOp",EDGE,"E32"),sQuery(id+"F0.wireOp",EDGE,"E33")])],"isStart":true}),makeQuery(id+"F2.opExtrude","CAP_FACE",FACE,{"disambiguationData":[OSD([subQ11,subQ10,subQ9,subQ8,subQ15,subQ14,subQ13,subQ12])],"isStart":true})]}),makeQuery(id+"F3.opExtrude","CAP_FACE",FACE,{"disambiguationData":[OSD([subQ11,subQ10,subQ9,subQ8])],"isStart":true})]}),makeQuery(id+"F6.opExtrude","CAP_FACE",FACE,{"disambiguationData":[OSD([subQ7,subQ6,sQuery(id+"F5.wireOp",EDGE,"E46"),sQuery(id+"F5.wireOp",EDGE,"E47"),sQuery(id+"F5.wireOp",EDGE,"VyiwcckC-eZpB-Ns7w-MLVF-TjthNmdLp171"),sQuery(id+"F5.wireOp",EDGE,"47fc8cb0-7b7c-463f-8738-2b292fe60b7a0.MirrorCS")])],"isStart":true})]}),makeQuery(id+"F7.opExtrude","CAP_FACE",FACE,{"disambiguationData":[OSD([subQ5,subQ4,sQuery(id+"F5.wireOp",EDGE,"E49"),sQuery(id+"F5.wireOp",EDGE,"E50"),sQuery(id+"F5.wireOp",EDGE,"9ff1a962-2a44-446a-a701-eef2fafc3d29"),sQuery(id+"F5.wireOp",EDGE,"3d39e784-e424-4d79-a023-b1c7c5447e9a.MirrorCS")])],"isStart":true}),makeQuery(id+"F7.opExtrude","CAP_FACE",FACE,{"disambiguationData":[OSD([subQ3,subQ2,sQuery(id+"F5.wireOp",EDGE,"E51"),sQuery(id+"F5.wireOp",EDGE,"E52"),sQuery(id+"F5.wireOp",EDGE,"61715c0d-76a2-4f19-8c7d-4868fa988be3"),sQuery(id+"F5.wireOp",EDGE,"6347a85b-d320-4235-87b3-466630833275.MirrorCS")])],"isStart":true}),makeQuery(id+"F7.opExtrude","CAP_FACE",FACE,{"disambiguationData":[OSD([subQ1,subQ0,sQuery(id+"F5.wireOp",EDGE,"E53"),sQuery(id+"F5.wireOp",EDGE,"E54"),sQuery(id+"F5.wireOp",EDGE,"51958e25-218a-4250-a5e8-a469592214fb"),sQuery(id+"F5.wireOp",EDGE,"2b9b2cda-c36c-46c9-b2f3-9b1550c60cb7.MirrorCS")])],"isStart":true})]});}
            var sketch = newSketch(context, id + "F9", { "sketchPlane" : qUnion([Q0])});
            skCircle(sketch, "E55", {"center": v(-96.86, 121.89) * mm, "radius": 16.11 * mm});
            skCircle(sketch, "E56", {"center": v(96.89, 121.86) * mm, "radius": 16.58 * mm});
            skCircle(sketch, "E57", {"center": v(96.89, 121.86) * mm, "radius": 16.77 * mm});
            skCircle(sketch, "E58", {"center": v(-96.89, -121.86) * mm, "radius": 15.86 * mm});
            skSolve(sketch);
        }
        {
            var Q0;
            Q0 = qSketchRegion(id + "F9", true);
            extrude(context, id + "F10", {"entities" : qUnion([Q0]), "operationType" : NewBodyOperationType.ADD, "oppositeDirection" : true, "depth" : 1 * mm, "offsetDistance" : 25 * mm});
        }
        {
            var Q0;
            {var subQ0=sQuery(id+"F4.wireOp",EDGE,"E44");var subQ1=sQuery(id+"F4.wireOp",EDGE,"E45");var subQ2=sQuery(id+"F4.wireOp",EDGE,"E43.MirrorCS");var subQ3=sQuery(id+"F4.wireOp",EDGE,"E41");var subQ4=sQuery(id+"F4.wireOp",EDGE,"E40");var subQ5=sQuery(id+"F4.wireOp",EDGE,"E39");Q0=makeQuery(id+"F7.boolean.opBoolean","SPLIT",FACE,{"disambiguationData":[TD([makeQuery(id+"F2.opExtrude","SWEPT_FACE",FACE,{"disambiguationData":[OSD([sQuery(id+"F0.wireOp",EDGE,"E4")])]})])],"derivedFrom":makeQuery(id+"F7.opExtrude","CAP_FACE",FACE,{"disambiguationData":[OSD([sQuery(id+"F0.wireOp",EDGE,"E0.top"),sQuery(id+"F0.wireOp",EDGE,"E16"),sQuery(id+"F0.wireOp",EDGE,"E20"),sQuery(id+"F0.wireOp",EDGE,"E22"),sQuery(id+"F0.wireOp",EDGE,"E24"),sQuery(id+"F0.wireOp",EDGE,"E26"),sQuery(id+"F0.wireOp",EDGE,"E28"),sQuery(id+"F0.wireOp",EDGE,"E30"),sQuery(id+"F0.wireOp",EDGE,"E31"),sQuery(id+"F0.wireOp",EDGE,"E32"),sQuery(id+"F0.wireOp",EDGE,"E33"),sQuery(id+"F4.wireOp",EDGE,"E37"),subQ5,subQ4,subQ3,sQuery(id+"F4.wireOp",EDGE,"E42.MirrorCS"),subQ2,subQ0,subQ1,sQuery(id+"F5.wireOp",EDGE,"E46"),sQuery(id+"F5.wireOp",EDGE,"E47"),sQuery(id+"F5.wireOp",EDGE,"E49"),sQuery(id+"F5.wireOp",EDGE,"E50"),sQuery(id+"F5.wireOp",EDGE,"9ff1a962-2a44-446a-a701-eef2fafc3d29"),sQuery(id+"F5.wireOp",EDGE,"E51"),sQuery(id+"F5.wireOp",EDGE,"E52"),sQuery(id+"F5.wireOp",EDGE,"E53"),sQuery(id+"F5.wireOp",EDGE,"E54")])],"isStart":false})});}
            extrude(context, id + "F11", {"entities" : qUnion([Q0]), "operationType" : NewBodyOperationType.REMOVE, "oppositeDirection" : true, "depth" : 17 * mm, "offsetDistance" : 25 * mm});
        }
        {
            var Q0;
            {var subQ0=sQuery(id+"F0.wireOp",EDGE,"E30");var subQ1=sQuery(id+"F0.wireOp",EDGE,"E29");var subQ2=sQuery(id+"F0.wireOp",EDGE,"E28");Q0=makeQuery(id+"F6.boolean.opBoolean","SPLIT",FACE,{"disambiguationData":[TD([makeQuery(id+"F1.opExtrude","SWEPT_FACE",FACE,{"disambiguationData":[OSD([subQ2])]})])],"derivedFrom":makeQuery(id+"F1.opExtrude","CAP_FACE",FACE,{"disambiguationData":[OSD([sQuery(id+"F0.wireOp",EDGE,"E0.top"),sQuery(id+"F0.wireOp",EDGE,"E9"),sQuery(id+"F0.wireOp",EDGE,"E10"),sQuery(id+"F0.wireOp",EDGE,"E11"),sQuery(id+"F0.wireOp",EDGE,"E12"),sQuery(id+"F0.wireOp",EDGE,"E16"),sQuery(id+"F0.wireOp",EDGE,"E17"),sQuery(id+"F0.wireOp",EDGE,"E18"),sQuery(id+"F0.wireOp",EDGE,"E19"),sQuery(id+"F0.wireOp",EDGE,"E20"),sQuery(id+"F0.wireOp",EDGE,"E22"),sQuery(id+"F0.wireOp",EDGE,"E23"),sQuery(id+"F0.wireOp",EDGE,"E24"),sQuery(id+"F0.wireOp",EDGE,"E26"),subQ2,subQ1,subQ0,sQuery(id+"F0.wireOp",EDGE,"E31"),sQuery(id+"F0.wireOp",EDGE,"E32"),sQuery(id+"F0.wireOp",EDGE,"E33")])],"isStart":false})});}
            var Q1;
            {var subQ0=sQuery(id+"F0.wireOp",EDGE,"E22");var subQ1=sQuery(id+"F0.wireOp",EDGE,"E20");var subQ2=sQuery(id+"F0.wireOp",EDGE,"E19");Q1=makeQuery(id+"F6.boolean.opBoolean","SPLIT",FACE,{"disambiguationData":[TD([makeQuery(id+"F1.opExtrude","SWEPT_FACE",FACE,{"disambiguationData":[OSD([subQ2])]})])],"derivedFrom":makeQuery(id+"F1.opExtrude","CAP_FACE",FACE,{"disambiguationData":[OSD([sQuery(id+"F0.wireOp",EDGE,"E0.top"),sQuery(id+"F0.wireOp",EDGE,"E9"),sQuery(id+"F0.wireOp",EDGE,"E10"),sQuery(id+"F0.wireOp",EDGE,"E11"),sQuery(id+"F0.wireOp",EDGE,"E12"),sQuery(id+"F0.wireOp",EDGE,"E16"),sQuery(id+"F0.wireOp",EDGE,"E17"),sQuery(id+"F0.wireOp",EDGE,"E18"),subQ2,subQ1,subQ0,sQuery(id+"F0.wireOp",EDGE,"E23"),sQuery(id+"F0.wireOp",EDGE,"E24"),sQuery(id+"F0.wireOp",EDGE,"E26"),sQuery(id+"F0.wireOp",EDGE,"E28"),sQuery(id+"F0.wireOp",EDGE,"E29"),sQuery(id+"F0.wireOp",EDGE,"E30"),sQuery(id+"F0.wireOp",EDGE,"E31"),sQuery(id+"F0.wireOp",EDGE,"E32"),sQuery(id+"F0.wireOp",EDGE,"E33")])],"isStart":false})});}
            var Q2;
            {var subQ0=sQuery(id+"F0.wireOp",EDGE,"E18");var subQ1=sQuery(id+"F0.wireOp",EDGE,"E17");var subQ2=sQuery(id+"F0.wireOp",EDGE,"E16");Q2=makeQuery(id+"F6.boolean.opBoolean","SPLIT",FACE,{"disambiguationData":[TD([makeQuery(id+"F1.opExtrude","SWEPT_FACE",FACE,{"disambiguationData":[OSD([subQ2])]})])],"derivedFrom":makeQuery(id+"F1.opExtrude","CAP_FACE",FACE,{"disambiguationData":[OSD([sQuery(id+"F0.wireOp",EDGE,"E0.top"),sQuery(id+"F0.wireOp",EDGE,"E9"),sQuery(id+"F0.wireOp",EDGE,"E10"),sQuery(id+"F0.wireOp",EDGE,"E11"),sQuery(id+"F0.wireOp",EDGE,"E12"),subQ2,subQ1,subQ0,sQuery(id+"F0.wireOp",EDGE,"E19"),sQuery(id+"F0.wireOp",EDGE,"E20"),sQuery(id+"F0.wireOp",EDGE,"E22"),sQuery(id+"F0.wireOp",EDGE,"E23"),sQuery(id+"F0.wireOp",EDGE,"E24"),sQuery(id+"F0.wireOp",EDGE,"E26"),sQuery(id+"F0.wireOp",EDGE,"E28"),sQuery(id+"F0.wireOp",EDGE,"E29"),sQuery(id+"F0.wireOp",EDGE,"E30"),sQuery(id+"F0.wireOp",EDGE,"E31"),sQuery(id+"F0.wireOp",EDGE,"E32"),sQuery(id+"F0.wireOp",EDGE,"E33")])],"isStart":false})});}
            extrude(context, id + "F12", {"entities" : qUnion([Q0, Q1, Q2]), "operationType" : NewBodyOperationType.REMOVE, "oppositeDirection" : true, "depth" : 9 * mm, "offsetDistance" : 25 * mm});
        }
        {
            var Q0;
            {var subQ0=sQuery(id+"F5.wireOp",EDGE,"E46");var subQ1=sQuery(id+"F0.wireOp",EDGE,"E33");var subQ2=sQuery(id+"F0.wireOp",EDGE,"E32");var subQ3=sQuery(id+"F0.wireOp",EDGE,"E31");var subQ4=sQuery(id+"F0.wireOp",EDGE,"E30");var subQ5=sQuery(id+"F0.wireOp",EDGE,"E29");var subQ6=sQuery(id+"F0.wireOp",EDGE,"E28");var subQ7=sQuery(id+"F0.wireOp",EDGE,"E26");var subQ8=sQuery(id+"F0.wireOp",EDGE,"E24");var subQ9=sQuery(id+"F0.wireOp",EDGE,"E23");var subQ10=sQuery(id+"F0.wireOp",EDGE,"E22");var subQ11=sQuery(id+"F0.wireOp",EDGE,"E20");var subQ12=sQuery(id+"F0.wireOp",EDGE,"E19");var subQ13=sQuery(id+"F0.wireOp",EDGE,"E18");var subQ14=sQuery(id+"F0.wireOp",EDGE,"E17");var subQ15=sQuery(id+"F0.wireOp",EDGE,"E16");var subQ16=sQuery(id+"F0.wireOp",EDGE,"E12");var subQ17=sQuery(id+"F0.wireOp",EDGE,"E11");var subQ18=sQuery(id+"F0.wireOp",EDGE,"E10");var subQ19=sQuery(id+"F0.wireOp",EDGE,"E9");var subQ20=sQuery(id+"F0.wireOp",EDGE,"E0.top");var subQ21=sQuery(id+"F5.wireOp",EDGE,"E54");var subQ22=sQuery(id+"F5.wireOp",EDGE,"E52");var subQ23=sQuery(id+"F5.wireOp",EDGE,"E50");var subQ24=sQuery(id+"F5.wireOp",EDGE,"E47");var subQ25=sQuery(id+"F4.wireOp",EDGE,"E45");var subQ26=sQuery(id+"F4.wireOp",EDGE,"E44");var subQ27=sQuery(id+"F4.wireOp",EDGE,"E43.MirrorCS");var subQ28=sQuery(id+"F4.wireOp",EDGE,"E42.MirrorCS");var subQ29=sQuery(id+"F4.wireOp",EDGE,"E41");var subQ30=sQuery(id+"F4.wireOp",EDGE,"E40");var subQ31=sQuery(id+"F4.wireOp",EDGE,"E39");var subQ32=sQuery(id+"F4.wireOp",EDGE,"E37");var subQ33=sQuery(id+"F0.wireOp",EDGE,"E7");var subQ34=sQuery(id+"F0.wireOp",EDGE,"E6");var subQ35=sQuery(id+"F0.wireOp",EDGE,"E5");var subQ36=sQuery(id+"F0.wireOp",EDGE,"E4");Q0=makeQuery(id+"F9.imprint","IMPRINT",FACE,{"disambiguationData":[TD([[makeQuery(id+"F9.imprint","IMPRINT",EDGE,{"derivedFrom":makeQuery(id+"F8.boolean.opBoolean","INTERSECT",EDGE,{"derivedFrom":[makeQuery(id+"F7.boolean.opBoolean","MERGE",FACE,{"derivedFrom":[makeQuery(id+"F6.boolean.opBoolean","MERGE",FACE,{"derivedFrom":[makeQuery(id+"F3.boolean.opBoolean","MERGE",FACE,{"derivedFrom":[makeQuery(id+"F2.boolean.opBoolean","MERGE",FACE,{"derivedFrom":[makeQuery(id+"F1.opExtrude","CAP_FACE",FACE,{"disambiguationData":[OSD([subQ20,subQ19,subQ18,subQ17,subQ16,subQ15,subQ14,subQ13,subQ12,subQ11,subQ10,subQ9,subQ8,subQ7,subQ6,subQ5,subQ4,subQ3,subQ2,subQ1])],"isStart":true}),makeQuery(id+"F2.opExtrude","CAP_FACE",FACE,{"disambiguationData":[OSD([subQ36,subQ35,subQ34,subQ33,subQ19,subQ18,subQ17,subQ16])],"isStart":true})]}),makeQuery(id+"F3.opExtrude","CAP_FACE",FACE,{"disambiguationData":[OSD([subQ36,subQ35,subQ34,subQ33])],"isStart":true})]}),makeQuery(id+"F6.opExtrude","CAP_FACE",FACE,{"disambiguationData":[OSD([subQ20,subQ15,subQ13,subQ11,subQ10,subQ8,subQ7,subQ6,subQ4,subQ3,subQ2,subQ1,subQ32,subQ31,subQ30,subQ29,subQ28,subQ27,subQ26,subQ25,subQ0,subQ24,subQ23,subQ22,subQ21])],"isStart":true})]}),makeQuery(id+"F7.opExtrude","CAP_FACE",FACE,{"disambiguationData":[OSD([subQ20,subQ15,subQ13,subQ11,subQ10,subQ8,subQ7,subQ6,subQ4,subQ3,subQ2,subQ1,subQ32,subQ31,subQ30,subQ29,subQ28,subQ27,subQ26,subQ25,subQ0,subQ24,sQuery(id+"F5.wireOp",EDGE,"E49"),subQ23,sQuery(id+"F5.wireOp",EDGE,"E51"),subQ22,sQuery(id+"F5.wireOp",EDGE,"E53"),subQ21])],"isStart":true})]}),makeQuery(id+"F8.opExtrude","SWEPT_FACE",FACE,{"disambiguationData":[OSD([subQ20,subQ19,subQ18,subQ17,subQ16,subQ15,subQ14,subQ13,subQ12,subQ11,subQ10,subQ9,subQ8,subQ7,subQ6,subQ5,subQ4,subQ3,subQ2,subQ1,subQ0])]})]})}),1.0]])]});}
            var Q1;
            {var subQ0=sQuery(id+"F0.wireOp",EDGE,"E19");Q1=makeQuery(id+"F9.imprint","IMPRINT",FACE,{"disambiguationData":[TD([[makeQuery(id+"F9.imprint","IMPRINT",EDGE,{"derivedFrom":makeQuery(id+"F1.opExtrude","CAP_EDGE",EDGE,{"disambiguationData":[OSD([subQ0])],"isStart":true})}),1.0]])]});}
            extrude(context, id + "F13", {"entities" : qUnion([Q0, Q1]), "operationType" : NewBodyOperationType.ADD, "oppositeDirection" : true, "depth" : 1 * mm, "offsetDistance" : 25 * mm});
        }
        {
            var Q0;
            {var subQ0=sQuery(id+"F5.wireOp",EDGE,"E54");var subQ1=sQuery(id+"F0.wireOp",EDGE,"E20");var subQ2=sQuery(id+"F5.wireOp",EDGE,"E47");var subQ3=sQuery(id+"F4.wireOp",EDGE,"E42.MirrorCS");var subQ4=sQuery(id+"F0.wireOp",EDGE,"E30");var subQ5=sQuery(id+"F0.wireOp",EDGE,"E16");var subQ6=sQuery(id+"F4.wireOp",EDGE,"E37");var subQ7=sQuery(id+"F4.wireOp",EDGE,"E44");var subQ8=sQuery(id+"F5.wireOp",EDGE,"E50");var subQ9=sQuery(id+"F0.wireOp",EDGE,"E31");var subQ10=sQuery(id+"F0.wireOp",EDGE,"E24");var subQ11=sQuery(id+"F4.wireOp",EDGE,"E41");var subQ12=sQuery(id+"F0.wireOp",EDGE,"E18");var subQ13=sQuery(id+"F5.wireOp",EDGE,"E53");var subQ14=sQuery(id+"F0.wireOp",EDGE,"E28");var subQ15=sQuery(id+"F5.wireOp",EDGE,"E52");var subQ16=sQuery(id+"F0.wireOp",EDGE,"E0.top");var subQ17=sQuery(id+"F0.wireOp",EDGE,"E26");var subQ18=sQuery(id+"F0.wireOp",EDGE,"E22");var subQ19=sQuery(id+"F4.wireOp",EDGE,"E45");var subQ20=sQuery(id+"F5.wireOp",EDGE,"E51");var subQ21=sQuery(id+"F0.wireOp",EDGE,"E33");var subQ22=sQuery(id+"F4.wireOp",EDGE,"E40");var subQ23=sQuery(id+"F5.wireOp",EDGE,"E49");var subQ24=sQuery(id+"F0.wireOp",EDGE,"E32");var subQ25=sQuery(id+"F5.wireOp",EDGE,"E46");Q0=makeQuery(id+"F7.boolean.opBoolean","SPLIT",FACE,{"disambiguationData":[TD([makeQuery(id+"F1.opExtrude","SWEPT_FACE",FACE,{"disambiguationData":[OSD([subQ16])]})])],"derivedFrom":makeQuery(id+"F7.opExtrude","CAP_FACE",FACE,{"disambiguationData":[OSD([subQ16,subQ5,subQ12,subQ1,subQ18,subQ10,subQ17,subQ14,subQ4,subQ9,subQ24,subQ21,subQ6,sQuery(id+"F4.wireOp",EDGE,"E39"),subQ22,subQ11,subQ3,sQuery(id+"F4.wireOp",EDGE,"E43.MirrorCS"),subQ7,subQ19,subQ25,subQ2,subQ23,subQ8,subQ20,subQ15,subQ13,subQ0])],"isStart":false})});}
            var sketch = newSketch(context, id + "F14", { "sketchPlane" : qUnion([Q0])});
            skLineSegment(sketch, "E59", {"start": v(-35, -42.32) * mm, "end": v(-35, -77.67) * mm});
            skLineSegment(sketch, "E60", {"start": v(-35, -77.67) * mm, "end": v(-70.36, -77.67) * mm});
            skLineSegment(sketch, "E61", {"start": v(-70.36, -77.67) * mm, "end": v(-70.36, -113.02) * mm});
            skLineSegment(sketch, "E62", {"start": v(-35, -42.32) * mm, "end": v(-94.7, -102) * mm});
            skLineSegment(sketch, "E63", {"start": v(-17.33, -60) * mm, "end": v(-35, -77.67) * mm});
            skLineSegment(sketch, "E64", {"start": v(-17.33, -60) * mm, "end": v(-52.69, -60) * mm});
            skLineSegment(sketch, "E65", {"start": v(-52.69, -60) * mm, "end": v(-52.69, -95.35) * mm});
            skLineSegment(sketch, "E66", {"start": v(-52.69, -95.35) * mm, "end": v(-88.05, -95.35) * mm});
            skLineSegment(sketch, "E67", {"start": v(-77, -119.64) * mm, "end": v(-70.36, -113.02) * mm});
            skLineSegment(sketch, "E68", {"start": v(-70.36, -113.02) * mm, "end": v(-35, -77.67) * mm});
            skCircle(sketch, "E69", {"center": v(-96.86, -121.89) * mm, "radius": 20 * mm});
            skLineSegment(sketch, "E70", {"start": v(-35, -42.32) * mm, "end": v(-35, -47.32) * mm, "construction": true});
            skLineSegment(sketch, "E71", {"start": v(-35, -47.32) * mm, "end": v(-90.6, -102.9) * mm});
            skLineSegment(sketch, "E72", {"start": v(-17.33, -60) * mm, "end": v(-22.33, -60) * mm, "construction": true});
            skLineSegment(sketch, "E73", {"start": v(-22.33, -60) * mm, "end": v(-77.9, -115.55) * mm, "construction": true});
            skLineSegment(sketch, "E74", {"start": v(-77.9, -115.55) * mm, "end": v(-22.33, -60) * mm});
            skCircle(sketch, "E75", {"center": v(-96.86, -121.89) * mm, "radius": 25 * mm});
            skLineSegment(sketch, "E76", {"start": v(-35, -56.47) * mm, "end": v(-38.54, -60) * mm});
            skLineSegment(sketch, "E77", {"start": v(-31.46, -60) * mm, "end": v(-35, -63.53) * mm});
            skPoint(sketch, "E78", {"position": v(-35, -60) * mm});
            skPoint(sketch, "E78.positionSnap0", {"position": v(-35, -60) * mm});
            skLineSegment(sketch, "E79", {"start": v(-52.69, -74.14) * mm, "end": v(-56.22, -77.67) * mm});
            skLineSegment(sketch, "E80", {"start": v(-49.14, -77.67) * mm, "end": v(-52.69, -81.2) * mm});
            skPoint(sketch, "E81", {"position": v(-52.69, -77.67) * mm});
            skLineSegment(sketch, "E82", {"start": v(-70.36, -91.8) * mm, "end": v(-73.9, -95.35) * mm});
            skLineSegment(sketch, "E83", {"start": v(-66.83, -95.35) * mm, "end": v(-70.36, -98.88) * mm});
            skPoint(sketch, "E84", {"position": v(-70.36, -95.34) * mm});
            skLineSegment(sketch, "E85", {"start": v(-73.9, -95.35) * mm, "end": v(-70.36, -98.88) * mm});
            skLineSegment(sketch, "E86", {"start": v(-70.36, -91.8) * mm, "end": v(-66.83, -95.35) * mm});
            skLineSegment(sketch, "E87", {"start": v(-52.69, -81.2) * mm, "end": v(-56.22, -77.67) * mm});
            skLineSegment(sketch, "E88", {"start": v(-52.69, -74.14) * mm, "end": v(-49.14, -77.67) * mm});
            skLineSegment(sketch, "E89", {"start": v(-35, -56.47) * mm, "end": v(-31.46, -60) * mm});
            skLineSegment(sketch, "E90", {"start": v(-35, -63.53) * mm, "end": v(-38.54, -60) * mm});
            skLineSegment(sketch, "E91", {"start": v(17.32, -60) * mm, "end": v(52.67, -60) * mm});
            skLineSegment(sketch, "E92", {"start": v(52.67, -60) * mm, "end": v(52.67, -95.36) * mm});
            skLineSegment(sketch, "E93", {"start": v(52.67, -95.36) * mm, "end": v(88.02, -95.36) * mm});
            skLineSegment(sketch, "E94", {"start": v(17.32, -60) * mm, "end": v(77, -119.7) * mm});
            skLineSegment(sketch, "E95", {"start": v(35, -42.32) * mm, "end": v(52.67, -60) * mm});
            skLineSegment(sketch, "E96", {"start": v(35, -42.32) * mm, "end": v(35, -77.68) * mm});
            skLineSegment(sketch, "E97", {"start": v(35, -77.68) * mm, "end": v(70.35, -77.68) * mm});
            skLineSegment(sketch, "E98", {"start": v(70.35, -77.68) * mm, "end": v(70.35, -113.04) * mm});
            skLineSegment(sketch, "E99", {"start": v(94.64, -101.98) * mm, "end": v(88.02, -95.36) * mm});
            skLineSegment(sketch, "E100", {"start": v(88.02, -95.36) * mm, "end": v(52.67, -60) * mm});
            skCircle(sketch, "E101", {"center": v(96.89, -121.86) * mm, "radius": 20 * mm});
            skLineSegment(sketch, "E102", {"start": v(17.32, -60) * mm, "end": v(22.32, -60) * mm, "construction": true});
            skLineSegment(sketch, "E103", {"start": v(22.32, -60) * mm, "end": v(77.9, -115.59) * mm});
            skLineSegment(sketch, "E104", {"start": v(35, -42.32) * mm, "end": v(35, -47.32) * mm, "construction": true});
            skLineSegment(sketch, "E105", {"start": v(35, -47.32) * mm, "end": v(90.55, -102.89) * mm, "construction": true});
            skLineSegment(sketch, "E106", {"start": v(90.55, -102.89) * mm, "end": v(35, -47.32) * mm});
            skCircle(sketch, "E107", {"center": v(96.89, -121.86) * mm, "radius": 25 * mm});
            skLineSegment(sketch, "E108", {"start": v(31.47, -60) * mm, "end": v(35, -63.53) * mm});
            skLineSegment(sketch, "E109", {"start": v(35, -56.46) * mm, "end": v(38.53, -60) * mm});
            skPoint(sketch, "E110", {"position": v(35, -60) * mm});
            skPoint(sketch, "E110.positionSnap0", {"position": v(35, -60) * mm});
            skLineSegment(sketch, "E111", {"start": v(49.14, -77.68) * mm, "end": v(52.67, -81.21) * mm});
            skLineSegment(sketch, "E112", {"start": v(52.67, -74.14) * mm, "end": v(56.2, -77.68) * mm});
            skPoint(sketch, "E113", {"position": v(52.67, -77.68) * mm});
            skLineSegment(sketch, "E114", {"start": v(66.8, -95.36) * mm, "end": v(70.35, -98.9) * mm});
            skLineSegment(sketch, "E115", {"start": v(70.35, -91.83) * mm, "end": v(73.88, -95.36) * mm});
            skPoint(sketch, "E116", {"position": v(70.34, -95.36) * mm});
            skLineSegment(sketch, "E117", {"start": v(70.35, -98.9) * mm, "end": v(73.88, -95.36) * mm});
            skLineSegment(sketch, "E118", {"start": v(66.8, -95.36) * mm, "end": v(70.35, -91.83) * mm});
            skLineSegment(sketch, "E119", {"start": v(56.2, -77.68) * mm, "end": v(52.67, -81.21) * mm});
            skLineSegment(sketch, "E120", {"start": v(49.14, -77.68) * mm, "end": v(52.67, -74.14) * mm});
            skLineSegment(sketch, "E121", {"start": v(31.47, -60) * mm, "end": v(35, -56.46) * mm});
            skLineSegment(sketch, "E122", {"start": v(38.53, -60) * mm, "end": v(35, -63.53) * mm});
            skLineSegment(sketch, "E123", {"start": v(35, 42.32) * mm, "end": v(35, 77.67) * mm});
            skLineSegment(sketch, "E124", {"start": v(35, 77.67) * mm, "end": v(70.36, 77.67) * mm});
            skLineSegment(sketch, "E125", {"start": v(70.36, 77.67) * mm, "end": v(70.36, 113.02) * mm});
            skLineSegment(sketch, "E126", {"start": v(35, 42.32) * mm, "end": v(94.7, 102) * mm});
            skLineSegment(sketch, "E127", {"start": v(17.33, 60) * mm, "end": v(35, 77.67) * mm});
            skLineSegment(sketch, "E128", {"start": v(17.33, 60) * mm, "end": v(52.69, 60) * mm});
            skLineSegment(sketch, "E129", {"start": v(52.69, 60) * mm, "end": v(52.69, 95.35) * mm});
            skLineSegment(sketch, "E130", {"start": v(52.69, 95.35) * mm, "end": v(88.05, 95.35) * mm});
            skLineSegment(sketch, "E131", {"start": v(77, 119.64) * mm, "end": v(70.36, 113.02) * mm});
            skLineSegment(sketch, "E132", {"start": v(70.36, 113.02) * mm, "end": v(35, 77.67) * mm});
            skCircle(sketch, "E133", {"center": v(96.86, 121.89) * mm, "radius": 20 * mm});
            skLineSegment(sketch, "E134", {"start": v(35, 42.32) * mm, "end": v(35, 47.32) * mm, "construction": true});
            skLineSegment(sketch, "E135", {"start": v(35, 47.32) * mm, "end": v(90.6, 102.9) * mm});
            skLineSegment(sketch, "E136", {"start": v(17.33, 60) * mm, "end": v(22.33, 60) * mm, "construction": true});
            skLineSegment(sketch, "E137", {"start": v(22.33, 60) * mm, "end": v(77.9, 115.55) * mm, "construction": true});
            skLineSegment(sketch, "E138", {"start": v(77.9, 115.55) * mm, "end": v(22.33, 60) * mm});
            skCircle(sketch, "E139", {"center": v(96.86, 121.89) * mm, "radius": 25 * mm});
            skLineSegment(sketch, "E140", {"start": v(35, 56.47) * mm, "end": v(38.54, 60) * mm});
            skLineSegment(sketch, "E141", {"start": v(31.46, 60) * mm, "end": v(35, 63.53) * mm});
            skPoint(sketch, "E142", {"position": v(35, 60) * mm});
            skPoint(sketch, "E142.positionSnap0", {"position": v(35, 60) * mm});
            skLineSegment(sketch, "E143", {"start": v(52.69, 74.14) * mm, "end": v(56.22, 77.67) * mm});
            skLineSegment(sketch, "E144", {"start": v(49.14, 77.67) * mm, "end": v(52.69, 81.2) * mm});
            skPoint(sketch, "E145", {"position": v(52.69, 77.67) * mm});
            skLineSegment(sketch, "E146", {"start": v(70.36, 91.8) * mm, "end": v(73.9, 95.35) * mm});
            skLineSegment(sketch, "E147", {"start": v(66.83, 95.35) * mm, "end": v(70.36, 98.88) * mm});
            skPoint(sketch, "E148", {"position": v(70.36, 95.34) * mm});
            skLineSegment(sketch, "E149", {"start": v(73.9, 95.35) * mm, "end": v(70.36, 98.88) * mm});
            skLineSegment(sketch, "E150", {"start": v(70.36, 91.8) * mm, "end": v(66.83, 95.35) * mm});
            skLineSegment(sketch, "E151", {"start": v(52.69, 81.2) * mm, "end": v(56.22, 77.67) * mm});
            skLineSegment(sketch, "E152", {"start": v(52.69, 74.14) * mm, "end": v(49.14, 77.67) * mm});
            skLineSegment(sketch, "E153", {"start": v(35, 56.47) * mm, "end": v(31.46, 60) * mm});
            skLineSegment(sketch, "E154", {"start": v(35, 63.53) * mm, "end": v(38.54, 60) * mm});
            skLineSegment(sketch, "E155", {"start": v(-17.32, 60) * mm, "end": v(-52.67, 60) * mm});
            skLineSegment(sketch, "E156", {"start": v(-52.67, 60) * mm, "end": v(-52.67, 95.36) * mm});
            skLineSegment(sketch, "E157", {"start": v(-52.67, 95.36) * mm, "end": v(-88.02, 95.36) * mm});
            skLineSegment(sketch, "E158", {"start": v(-17.32, 60) * mm, "end": v(-77, 119.7) * mm});
            skLineSegment(sketch, "E159", {"start": v(-35, 42.32) * mm, "end": v(-52.67, 60) * mm});
            skLineSegment(sketch, "E160", {"start": v(-35, 42.32) * mm, "end": v(-35, 77.68) * mm});
            skLineSegment(sketch, "E161", {"start": v(-35, 77.68) * mm, "end": v(-70.35, 77.68) * mm});
            skLineSegment(sketch, "E162", {"start": v(-70.35, 77.68) * mm, "end": v(-70.35, 113.04) * mm});
            skLineSegment(sketch, "E163", {"start": v(-94.64, 101.98) * mm, "end": v(-88.02, 95.36) * mm});
            skLineSegment(sketch, "E164", {"start": v(-88.02, 95.36) * mm, "end": v(-52.67, 60) * mm});
            skCircle(sketch, "E165", {"center": v(-96.89, 121.86) * mm, "radius": 20 * mm});
            skLineSegment(sketch, "E166", {"start": v(-17.32, 60) * mm, "end": v(-22.32, 60) * mm, "construction": true});
            skLineSegment(sketch, "E167", {"start": v(-22.32, 60) * mm, "end": v(-77.9, 115.59) * mm});
            skLineSegment(sketch, "E168", {"start": v(-35, 42.32) * mm, "end": v(-35, 47.32) * mm, "construction": true});
            skLineSegment(sketch, "E169", {"start": v(-35, 47.32) * mm, "end": v(-90.55, 102.89) * mm, "construction": true});
            skLineSegment(sketch, "E170", {"start": v(-90.55, 102.89) * mm, "end": v(-35, 47.32) * mm});
            skCircle(sketch, "E171", {"center": v(-96.89, 121.86) * mm, "radius": 25 * mm});
            skLineSegment(sketch, "E172", {"start": v(-31.47, 60) * mm, "end": v(-35, 63.53) * mm});
            skLineSegment(sketch, "E173", {"start": v(-35, 56.46) * mm, "end": v(-38.53, 60) * mm});
            skPoint(sketch, "E174", {"position": v(-35, 60) * mm});
            skPoint(sketch, "E174.positionSnap0", {"position": v(-35, 60) * mm});
            skLineSegment(sketch, "E175", {"start": v(-49.14, 77.68) * mm, "end": v(-52.67, 81.21) * mm});
            skLineSegment(sketch, "E176", {"start": v(-52.67, 74.14) * mm, "end": v(-56.2, 77.68) * mm});
            skPoint(sketch, "E177", {"position": v(-52.67, 77.68) * mm});
            skLineSegment(sketch, "E178", {"start": v(-66.8, 95.36) * mm, "end": v(-70.35, 98.9) * mm});
            skLineSegment(sketch, "E179", {"start": v(-70.35, 91.83) * mm, "end": v(-73.88, 95.36) * mm});
            skPoint(sketch, "E180", {"position": v(-70.34, 95.36) * mm});
            skLineSegment(sketch, "E181", {"start": v(-70.35, 98.9) * mm, "end": v(-73.88, 95.36) * mm});
            skLineSegment(sketch, "E182", {"start": v(-66.8, 95.36) * mm, "end": v(-70.35, 91.83) * mm});
            skLineSegment(sketch, "E183", {"start": v(-56.2, 77.68) * mm, "end": v(-52.67, 81.21) * mm});
            skLineSegment(sketch, "E184", {"start": v(-49.14, 77.68) * mm, "end": v(-52.67, 74.14) * mm});
            skLineSegment(sketch, "E185", {"start": v(-31.47, 60) * mm, "end": v(-35, 56.46) * mm});
            skLineSegment(sketch, "E186", {"start": v(-38.53, 60) * mm, "end": v(-35, 63.53) * mm});
            skSolve(sketch);
        }
        {
            var Q0;
            {var subQ0=sQuery(id+"F14.wireOp",EDGE,"E88");Q0=makeQuery(id+"F14.imprint","IMPRINT",FACE,{"disambiguationData":[TD([[makeQuery(id+"F14.imprint","IMPRINT",EDGE,{"derivedFrom":subQ0}),1.0]])]});}
            var Q1;
            {var subQ0=sQuery(id+"F14.wireOp",EDGE,"E86");Q1=makeQuery(id+"F14.imprint","IMPRINT",FACE,{"disambiguationData":[TD([[makeQuery(id+"F14.imprint","IMPRINT",EDGE,{"derivedFrom":subQ0}),1.0]])]});}
            var Q2;
            {var subQ9=sQuery(id+"F14.wireOp",EDGE,"E85");Q2=makeQuery(id+"F14.imprint","IMPRINT",FACE,{"disambiguationData":[TD([[makeQuery(id+"F14.imprint","IMPRINT",EDGE,{"derivedFrom":subQ9}),-1.0]])]});}
            var Q3;
            {var subQ0=sQuery(id+"F14.wireOp",EDGE,"E184");Q3=makeQuery(id+"F14.imprint","IMPRINT",FACE,{"disambiguationData":[TD([[makeQuery(id+"F14.imprint","IMPRINT",EDGE,{"derivedFrom":subQ0}),1.0]])]});}
            var Q4;
            {var subQ0=sQuery(id+"F14.wireOp",EDGE,"E182");Q4=makeQuery(id+"F14.imprint","IMPRINT",FACE,{"disambiguationData":[TD([[makeQuery(id+"F14.imprint","IMPRINT",EDGE,{"derivedFrom":subQ0}),1.0]])]});}
            var Q5;
            {var subQ5=sQuery(id+"F14.wireOp",EDGE,"E181");Q5=makeQuery(id+"F14.imprint","IMPRINT",FACE,{"disambiguationData":[TD([[makeQuery(id+"F14.imprint","IMPRINT",EDGE,{"derivedFrom":subQ5}),-1.0]])]});}
            var Q6;
            {var subQ0=sQuery(id+"F14.wireOp",EDGE,"E152");Q6=makeQuery(id+"F14.imprint","IMPRINT",FACE,{"disambiguationData":[TD([[makeQuery(id+"F14.imprint","IMPRINT",EDGE,{"derivedFrom":subQ0}),1.0]])]});}
            var Q7;
            {var subQ0=sQuery(id+"F14.wireOp",EDGE,"E150");Q7=makeQuery(id+"F14.imprint","IMPRINT",FACE,{"disambiguationData":[TD([[makeQuery(id+"F14.imprint","IMPRINT",EDGE,{"derivedFrom":subQ0}),1.0]])]});}
            var Q8;
            {var subQ9=sQuery(id+"F14.wireOp",EDGE,"E149");Q8=makeQuery(id+"F14.imprint","IMPRINT",FACE,{"disambiguationData":[TD([[makeQuery(id+"F14.imprint","IMPRINT",EDGE,{"derivedFrom":subQ9}),-1.0]])]});}
            var Q9;
            {var subQ0=sQuery(id+"F14.wireOp",EDGE,"E120");Q9=makeQuery(id+"F14.imprint","IMPRINT",FACE,{"disambiguationData":[TD([[makeQuery(id+"F14.imprint","IMPRINT",EDGE,{"derivedFrom":subQ0}),1.0]])]});}
            var Q10;
            {var subQ0=sQuery(id+"F14.wireOp",EDGE,"E118");Q10=makeQuery(id+"F14.imprint","IMPRINT",FACE,{"disambiguationData":[TD([[makeQuery(id+"F14.imprint","IMPRINT",EDGE,{"derivedFrom":subQ0}),1.0]])]});}
            var Q11;
            {var subQ5=sQuery(id+"F14.wireOp",EDGE,"E117");Q11=makeQuery(id+"F14.imprint","IMPRINT",FACE,{"disambiguationData":[TD([[makeQuery(id+"F14.imprint","IMPRINT",EDGE,{"derivedFrom":subQ5}),-1.0]])]});}
            extrude(context, id + "F15", {"entities" : qUnion([Q0, Q1, Q2, Q3, Q4, Q5, Q6, Q7, Q8, Q9, Q10, Q11]), "operationType" : NewBodyOperationType.REMOVE, "oppositeDirection" : true, "depth" : 25 * mm, "offsetDistance" : 25 * mm});
        }
        {
            var Q0;
            {var subQ0=sQuery(id+"F5.wireOp",EDGE,"E54");var subQ1=sQuery(id+"F0.wireOp",EDGE,"E20");var subQ2=sQuery(id+"F5.wireOp",EDGE,"E47");var subQ3=sQuery(id+"F4.wireOp",EDGE,"E42.MirrorCS");var subQ4=sQuery(id+"F0.wireOp",EDGE,"E30");var subQ5=sQuery(id+"F0.wireOp",EDGE,"E16");var subQ6=sQuery(id+"F4.wireOp",EDGE,"E37");var subQ7=sQuery(id+"F4.wireOp",EDGE,"E44");var subQ8=sQuery(id+"F5.wireOp",EDGE,"E50");var subQ9=sQuery(id+"F0.wireOp",EDGE,"E31");var subQ10=sQuery(id+"F0.wireOp",EDGE,"E24");var subQ11=sQuery(id+"F4.wireOp",EDGE,"E41");var subQ12=sQuery(id+"F0.wireOp",EDGE,"E18");var subQ13=sQuery(id+"F5.wireOp",EDGE,"E53");var subQ14=sQuery(id+"F0.wireOp",EDGE,"E28");var subQ15=sQuery(id+"F5.wireOp",EDGE,"E52");var subQ16=sQuery(id+"F0.wireOp",EDGE,"E0.top");var subQ17=sQuery(id+"F0.wireOp",EDGE,"E26");var subQ18=sQuery(id+"F0.wireOp",EDGE,"E22");var subQ19=sQuery(id+"F4.wireOp",EDGE,"E45");var subQ20=sQuery(id+"F5.wireOp",EDGE,"E51");var subQ21=sQuery(id+"F0.wireOp",EDGE,"E33");var subQ22=sQuery(id+"F4.wireOp",EDGE,"E40");var subQ23=sQuery(id+"F5.wireOp",EDGE,"E49");var subQ24=sQuery(id+"F0.wireOp",EDGE,"E32");var subQ25=sQuery(id+"F5.wireOp",EDGE,"E46");Q0=makeQuery(id+"F7.boolean.opBoolean","SPLIT",FACE,{"disambiguationData":[TD([makeQuery(id+"F1.opExtrude","SWEPT_FACE",FACE,{"disambiguationData":[OSD([subQ16])]})])],"derivedFrom":makeQuery(id+"F7.opExtrude","CAP_FACE",FACE,{"disambiguationData":[OSD([subQ16,subQ5,subQ12,subQ1,subQ18,subQ10,subQ17,subQ14,subQ4,subQ9,subQ24,subQ21,subQ6,sQuery(id+"F4.wireOp",EDGE,"E39"),subQ22,subQ11,subQ3,sQuery(id+"F4.wireOp",EDGE,"E43.MirrorCS"),subQ7,subQ19,subQ25,subQ2,subQ23,subQ8,subQ20,subQ15,subQ13,subQ0])],"isStart":false})});}
            var sketch = newSketch(context, id + "F16", { "sketchPlane" : qUnion([Q0])});
            skCircle(sketch, "E187", {"center": v(-96.89, 121.86) * mm, "radius": 20 * mm});
            skCircle(sketch, "E188", {"center": v(96.86, 121.89) * mm, "radius": 20 * mm});
            skCircle(sketch, "E189", {"center": v(96.89, -121.86) * mm, "radius": 20 * mm});
            skCircle(sketch, "E190", {"center": v(-96.86, -121.89) * mm, "radius": 20 * mm});
            skLineSegment(sketch, "E191.bottom", {"start": v(-29.52, 50.6) * mm, "end": v(29.52, 50.6) * mm});
            skLineSegment(sketch, "E191.top", {"start": v(-29.52, -50.6) * mm, "end": v(29.52, -50.6) * mm});
            skLineSegment(sketch, "E191.left", {"start": v(-29.52, 50.6) * mm, "end": v(-29.52, -50.6) * mm});
            skLineSegment(sketch, "E191.right", {"start": v(29.52, 50.6) * mm, "end": v(29.52, -50.6) * mm});
            skSolve(sketch);
        }
        {
            var Q0;
            Q0=makeQuery(id+"F16.imprint","IMPRINT",FACE,{"disambiguationData":[TD([[makeQuery(id+"F16.imprint","IMPRINT",EDGE,{"disambiguationData":[OD(1.0)],"derivedFrom":sQuery(id+"F16.wireOp",EDGE,"E187")}),-1.0]])]});
            extrude(context, id + "F17", {"entities" : qUnion([Q0]), "operationType" : NewBodyOperationType.REMOVE, "oppositeDirection" : true, "depth" : 7.5 * mm, "offsetDistance" : 25 * mm});
        }
    });
